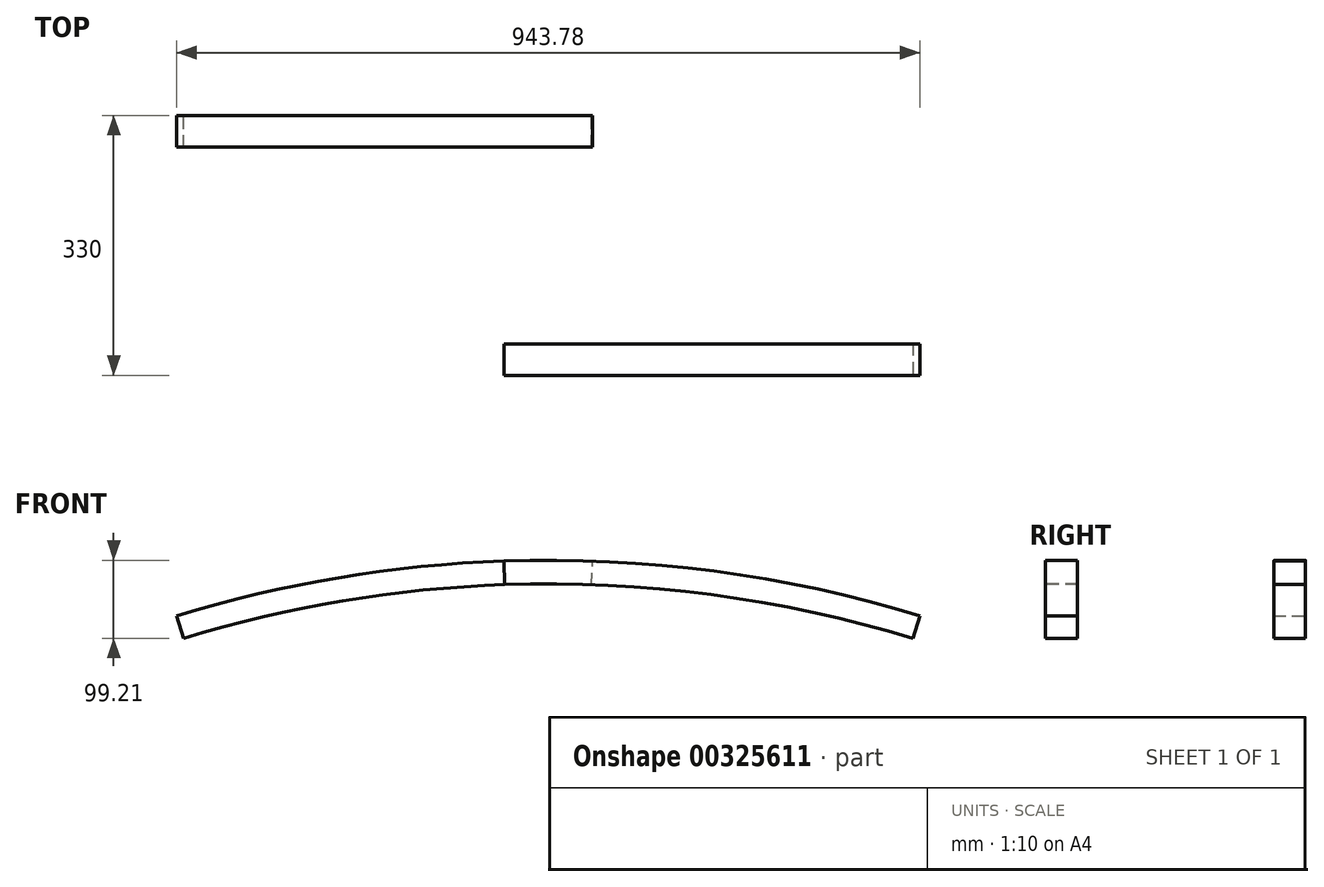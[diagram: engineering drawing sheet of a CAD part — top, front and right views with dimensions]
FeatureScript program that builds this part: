
annotation { "Feature Type Name" : "Feature", "Feature Type Description" : "" }
export const myFeature = defineFeature(function(context is Context, id is Id, definition is map)
    precondition{}
    {
        {
            var Q0;
            Q0=qCreatedBy(makeId("Right.planeOp"),FACE);
            var sketch = newSketch(context, id + "F0", { "sketchPlane" : qUnion([Q0])});
            skLineSegment(sketch, "E0", {"start": v(-75.2, 0) * mm, "end": v(74.8, 0) * mm, "construction": true});
            skLineSegment(sketch, "E1.bottom", {"start": v(200, 1554) * mm, "end": v(-200, 1554) * mm});
            skLineSegment(sketch, "E1.top", {"start": v(200, 1584) * mm, "end": v(-200, 1584) * mm});
            skLineSegment(sketch, "E1.left", {"start": v(200, 1554) * mm, "end": v(200, 1584) * mm});
            skLineSegment(sketch, "E1.right", {"start": v(-200, 1554) * mm, "end": v(-200, 1584) * mm});
            skPoint(sketch, "E1.middle", {"position": v(0, 1569) * mm});
            skSolve(sketch);
        }
        {
            var Q0;
            Q0=qCreatedBy(makeId("Top.planeOp"),FACE);
            cPlane(context, id + "F1", {"entities" : qUnion([Q0]), "cplaneType" : CPlaneType.OFFSET, "offset" : 1600 * mm, "width" : 150 * mm, "height" : 150 * mm});
        }
        {
            var Q0;
            Q0=qCreatedBy(id+"F1.planeOp",FACE);
            var sketch = newSketch(context, id + "F2", { "sketchPlane" : qUnion([Q0])});
            skCircle(sketch, "E2", {"center": v(-100, 225) * mm, "radius": 3 * mm});
            skLineSegment(sketch, "E3", {"start": v(150.49, 0) * mm, "end": v(-149.91, 0) * mm, "construction": true});
            skLineSegment(sketch, "E4", {"start": v(0, 158.55) * mm, "end": v(0, -163.66) * mm, "construction": true});
            skPoint(sketch, "E5", {"position": v(0, 0) * mm});
            skSolve(sketch);
        }
        {
            var Q0;
            Q0=qCreatedBy(makeId("Right.planeOp"),FACE);
            var sketch = newSketch(context, id + "F3", { "sketchPlane" : qUnion([Q0])});
            skLineSegment(sketch, "E6.bottom", {"start": v(-125, 1584) * mm, "end": v(-165, 1584) * mm});
            skLineSegment(sketch, "E6.top", {"start": v(-125, 1614) * mm, "end": v(-165, 1614) * mm});
            skLineSegment(sketch, "E6.left", {"start": v(-125, 1584) * mm, "end": v(-125, 1614) * mm});
            skLineSegment(sketch, "E6.right", {"start": v(-165, 1584) * mm, "end": v(-165, 1614) * mm});
            skPoint(sketch, "E6.middle", {"position": v(-145, 1599) * mm});
            skLineSegment(sketch, "E7", {"start": v(0, 1548.3) * mm, "end": v(0, 1675.11) * mm, "construction": true});
            skLineSegment(sketch, "E8.MirrorCS", {"start": v(125, 1614) * mm, "end": v(165, 1614) * mm});
            skLineSegment(sketch, "E9.MirrorCS", {"start": v(125, 1584) * mm, "end": v(125, 1614) * mm});
            skLineSegment(sketch, "E10.MirrorCS", {"start": v(125, 1584) * mm, "end": v(165, 1584) * mm});
            skLineSegment(sketch, "E11.MirrorCS", {"start": v(165, 1584) * mm, "end": v(165, 1614) * mm});
            skPoint(sketch, "E12.MirrorP", {"position": v(145, 1599) * mm});
            skSolve(sketch);
        }
        {
            var Q0;
            Q0=makeQuery(id+"F3.imprint","IMPRINT",FACE,{"disambiguationData":[TD([[makeQuery(id+"F3.imprint","IMPRINT",EDGE,{"derivedFrom":sQuery(id+"F3.wireOp",EDGE,"E6.bottom")}),-1.0]])]});
            var Q1;
            Q1=sQuery(id+"F0.wireOp",EDGE,"E0");
            revolve(context, id + "F4", {"entities" : qUnion([Q0]), "axis" : qUnion([Q1]), "revolveType" : RevolveType.TWO_DIRECTIONS, "angle" : 17 * degree, "angleBack" : 358 * degree});
        }
        {
            var Q0;
            Q0=makeQuery(id+"F3.imprint","IMPRINT",FACE,{"disambiguationData":[TD([[makeQuery(id+"F3.imprint","IMPRINT",EDGE,{"derivedFrom":sQuery(id+"F3.wireOp",EDGE,"E8.MirrorCS")}),-1.0]])]});
            var Q1;
            Q1=sQuery(id+"F0.wireOp",EDGE,"E0");
            revolve(context, id + "F5", {"entities" : qUnion([Q0]), "axis" : qUnion([Q1]), "revolveType" : RevolveType.TWO_DIRECTIONS, "oppositeDirection" : true, "angle" : 17 * degree, "angleBack" : 358 * degree});
        }
    });
